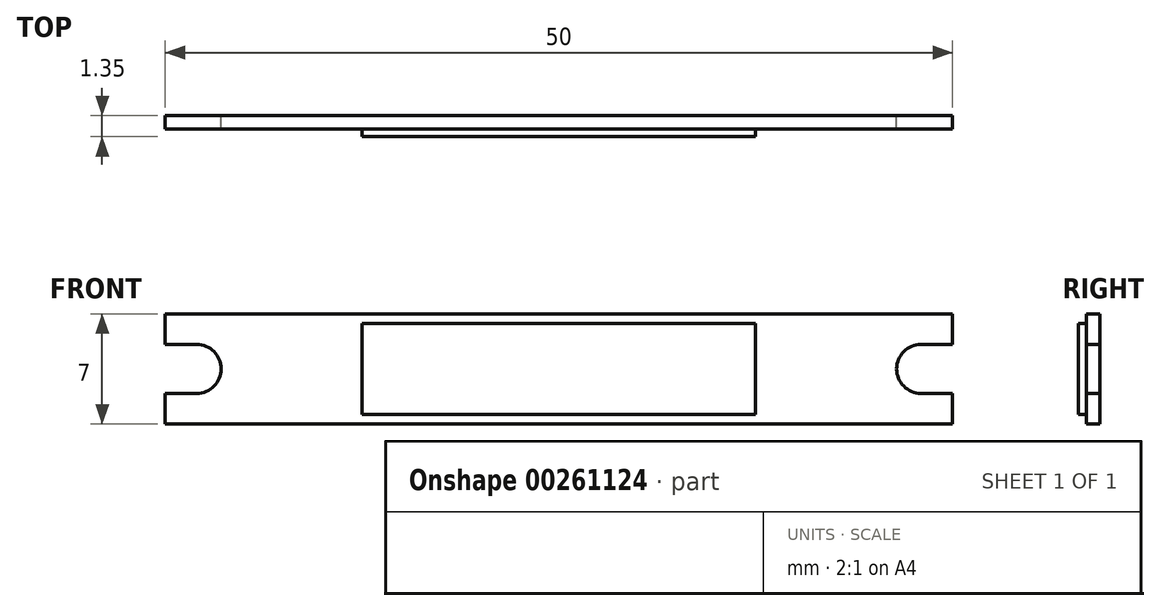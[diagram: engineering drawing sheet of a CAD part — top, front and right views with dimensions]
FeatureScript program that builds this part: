
annotation { "Feature Type Name" : "Feature", "Feature Type Description" : "" }
export const myFeature = defineFeature(function(context is Context, id is Id, definition is map)
    precondition{}
    {
        {
            var Q0;
            Q0=qCreatedBy(makeId("Front.planeOp"),FACE);
            var sketch = newSketch(context, id + "F0", { "sketchPlane" : qUnion([Q0])});
            skLineSegment(sketch, "E0.bottom", {"start": v(25, 3.5) * mm, "end": v(-25, 3.5) * mm});
            skLineSegment(sketch, "E0.top", {"start": v(25, -3.5) * mm, "end": v(-25, -3.5) * mm});
            skLineSegment(sketch, "E0.left", {"start": v(25, 3.5) * mm, "end": v(25, 1.55) * mm});
            skLineSegment(sketch, "E0.right", {"start": v(-25, 3.5) * mm, "end": v(-25, 1.55) * mm});
            skPoint(sketch, "E0.middle", {"position": v(0, 0) * mm});
            skLineSegment(sketch, "E1.bottom", {"start": v(12.5, 2.9) * mm, "end": v(-12.5, 2.9) * mm});
            skLineSegment(sketch, "E1.top", {"start": v(12.5, -2.9) * mm, "end": v(-12.5, -2.9) * mm});
            skLineSegment(sketch, "E1.left", {"start": v(12.5, 2.9) * mm, "end": v(12.5, -2.9) * mm});
            skLineSegment(sketch, "E1.right", {"start": v(-12.5, 2.9) * mm, "end": v(-12.5, -2.9) * mm});
            skArc(sketch, "E2", {"start": v(-23, -1.55) * mm, "mid": v(-21.45, 0) * mm, "end": v(-23, 1.55) * mm});
            skArc(sketch, "E3", {"start": v(23, 1.55) * mm, "mid": v(21.45, 0) * mm, "end": v(23, -1.55) * mm});
            skPoint(sketch, "E4", {"position": v(-21.45, 0) * mm});
            skPoint(sketch, "E4.positionSnap0", {"position": v(-12.5, 0) * mm});
            skPoint(sketch, "E5", {"position": v(21.45, 0) * mm});
            skLineSegment(sketch, "E6", {"start": v(-23, 1.55) * mm, "end": v(-25, 1.55) * mm});
            skLineSegment(sketch, "E7", {"start": v(-23, -1.55) * mm, "end": v(-25, -1.55) * mm});
            skLineSegment(sketch, "E8", {"start": v(23, 1.55) * mm, "end": v(25, 1.55) * mm});
            skLineSegment(sketch, "E9", {"start": v(23, -1.55) * mm, "end": v(25, -1.55) * mm});
            skLineSegment(sketch, "E10.trimOffspring", {"start": v(-25, -1.55) * mm, "end": v(-25, -3.5) * mm});
            skLineSegment(sketch, "E11.trimOffspring", {"start": v(25, -1.55) * mm, "end": v(25, -3.5) * mm});
            skSolve(sketch);
        }
        {
            var Q0;
            Q0=makeQuery(id+"F0.imprint","IMPRINT",FACE,{"disambiguationData":[TD([[makeQuery(id+"F0.imprint","IMPRINT",EDGE,{"derivedFrom":sQuery(id+"F0.wireOp",EDGE,"E1.bottom")}),1.0]])]});
            extrude(context, id + "F1", {"entities" : qUnion([Q0]), "depth" : 1.35 * mm});
        }
        {
            var Q0;
            Q0 = qSketchRegion(id + "F0", true);
            extrude(context, id + "F2", {"entities" : qUnion([Q0]), "operationType" : NewBodyOperationType.ADD, "depth" : .85 * mm});
        }
    });
